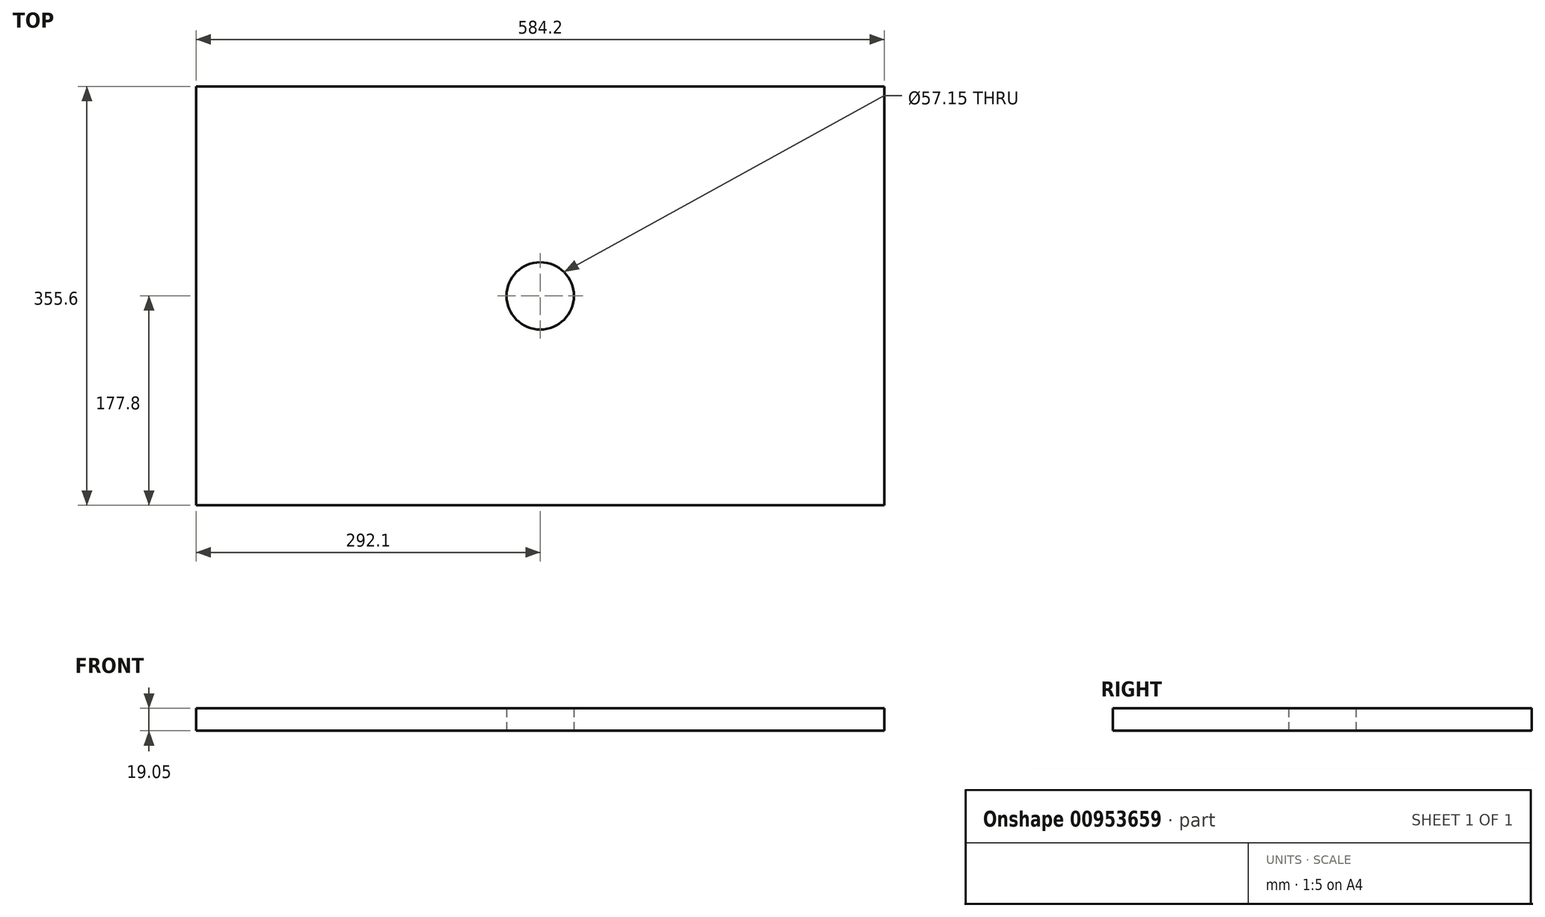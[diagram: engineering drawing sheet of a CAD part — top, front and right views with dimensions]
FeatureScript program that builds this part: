
annotation { "Feature Type Name" : "Feature", "Feature Type Description" : "" }
export const myFeature = defineFeature(function(context is Context, id is Id, definition is map)
    precondition{}
    {
        {
            var Q0;
            Q0=qCreatedBy(makeId("Top.planeOp"),FACE);
            var sketch = newSketch(context, id + "F0", { "sketchPlane" : qUnion([Q0])});
            skPoint(sketch, "E0.middle", {"position": v(0, 0) * mm});
            skCircle(sketch, "E1", {"center": v(0, 0) * mm, "radius": 28.58 * mm});
            skLineSegment(sketch, "E2.bottom", {"start": v(292.1, -177.8) * mm, "end": v(-292.1, -177.8) * mm});
            skLineSegment(sketch, "E2.top", {"start": v(292.1, 177.8) * mm, "end": v(-292.1, 177.8) * mm});
            skLineSegment(sketch, "E2.left", {"start": v(292.1, -177.8) * mm, "end": v(292.1, 177.8) * mm});
            skLineSegment(sketch, "E2.right", {"start": v(-292.1, -177.8) * mm, "end": v(-292.1, 177.8) * mm});
            skSolve(sketch);
        }
        {
            var Q0;
            Q0=makeQuery(id+"F0.imprint","IMPRINT",FACE,{"disambiguationData":[TD([[makeQuery(id+"F0.imprint","IMPRINT",EDGE,{"derivedFrom":sQuery(id+"F0.wireOp",EDGE,"E1")}),-1.0]])]});
            extrude(context, id + "F1", {"entities" : qUnion([Q0]), "depth" : 19.05 * mm, "offsetDistance" : 25.4 * mm});
        }
    });
